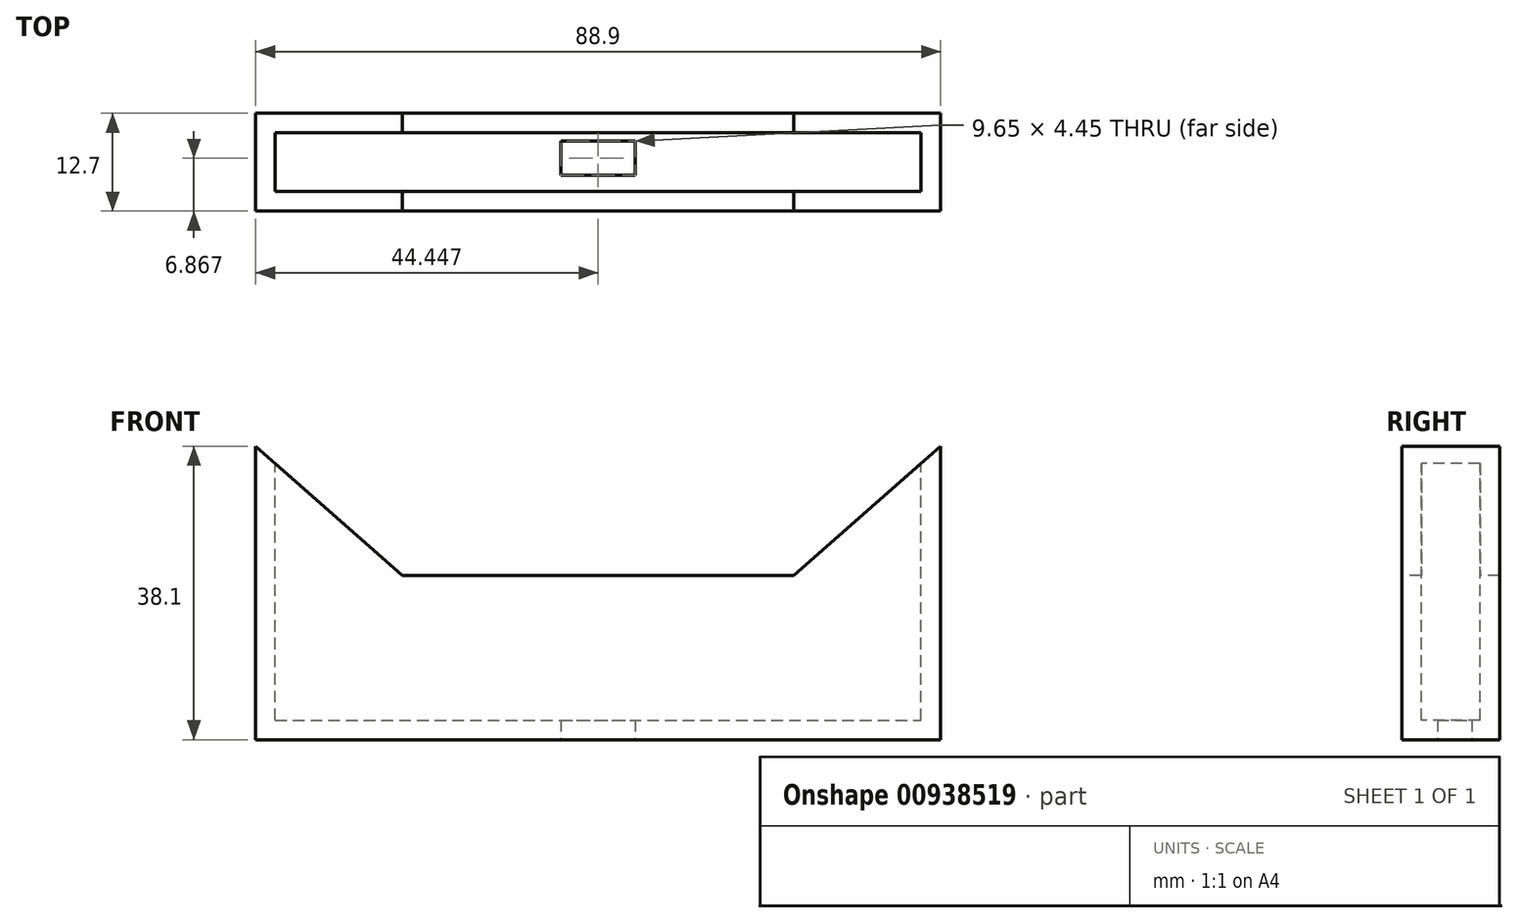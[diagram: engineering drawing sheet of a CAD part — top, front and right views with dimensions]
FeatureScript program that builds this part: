
annotation { "Feature Type Name" : "Feature", "Feature Type Description" : "" }
export const myFeature = defineFeature(function(context is Context, id is Id, definition is map)
    precondition{}
    {
        {
            var Q0;
            Q0=qCreatedBy(makeId("Front.planeOp"),FACE);
            var sketch = newSketch(context, id + "F0", { "sketchPlane" : qUnion([Q0])});
            skLineSegment(sketch, "E0", {"start": v(-47.41, 0) * mm, "end": v(41.49, 0) * mm});
            skLineSegment(sketch, "E1", {"start": v(41.49, 0) * mm, "end": v(41.49, 38.1) * mm});
            skLineSegment(sketch, "E2", {"start": v(-47.41, 0) * mm, "end": v(-47.41, 38.1) * mm});
            skLineSegment(sketch, "E3", {"start": v(-47.41, 38.1) * mm, "end": v(-28.36, 21.3) * mm});
            skLineSegment(sketch, "E4", {"start": v(-28.36, 21.3) * mm, "end": v(22.44, 21.3) * mm});
            skLineSegment(sketch, "E5", {"start": v(22.44, 21.3) * mm, "end": v(41.49, 38.1) * mm});
            skSolve(sketch);
        }
        {
            var Q0;
            Q0=makeQuery(id+"F0.imprint","IMPRINT",FACE,{"disambiguationData":[TD([[makeQuery(id+"F0.imprint","IMPRINT",EDGE,{"derivedFrom":sQuery(id+"F0.wireOp",EDGE,"E0")}),1.0]])]});
            extrude(context, id + "F1", {"entities" : qUnion([Q0]), "oppositeDirection" : true, "depth" : 12.7 * mm, "offsetDistance" : 25.4 * mm});
        }
        {
            var Q0;
            Q0=makeQuery(id+"F1.opExtrude","SWEPT_FACE",FACE,{"disambiguationData":[OSD([sQuery(id+"F0.wireOp",EDGE,"E4")])]});
            var Q1;
            Q1=makeQuery(id+"F1.opExtrude","SWEPT_FACE",FACE,{"disambiguationData":[OSD([sQuery(id+"F0.wireOp",EDGE,"E3")])]});
            var Q2;
            Q2=makeQuery(id+"F1.opExtrude","SWEPT_FACE",FACE,{"disambiguationData":[OSD([sQuery(id+"F0.wireOp",EDGE,"E5")])]});
            shell(context, id + "F2", {"entities" : qUnion([Q0, Q1, Q2]), "thickness" : 2.54 * mm});
        }
        {
            var Q0;
            Q0=qCreatedBy(makeId("Top.planeOp"),FACE);
            var sketch = newSketch(context, id + "F3", { "sketchPlane" : qUnion([Q0])});
            skLineSegment(sketch, "E6.bottom", {"start": v(-7.79, 4.64) * mm, "end": v(1.86, 4.64) * mm});
            skLineSegment(sketch, "E6.top", {"start": v(-7.79, 9.09) * mm, "end": v(1.86, 9.09) * mm});
            skLineSegment(sketch, "E6.left", {"start": v(-7.79, 4.64) * mm, "end": v(-7.79, 9.09) * mm});
            skLineSegment(sketch, "E6.right", {"start": v(1.86, 4.64) * mm, "end": v(1.86, 9.09) * mm});
            skLineSegment(sketch, "E7", {"start": v(-7.79, 9.09) * mm, "end": v(-47.41, 9.09) * mm, "construction": true});
            skLineSegment(sketch, "E8", {"start": v(1.86, 9.09) * mm, "end": v(41.49, 9.09) * mm, "construction": true});
            skSolve(sketch);
        }
        {
            var Q0;
            Q0=makeQuery(id+"F3.imprint","IMPRINT",FACE,{"disambiguationData":[TD([[makeQuery(id+"F3.imprint","IMPRINT",EDGE,{"derivedFrom":sQuery(id+"F3.wireOp",EDGE,"E6.bottom")}),1.0]])]});
            extrude(context, id + "F4", {"entities" : qUnion([Q0]), "operationType" : NewBodyOperationType.REMOVE, "depth" : 25.4 * mm, "offsetDistance" : 25.4 * mm});
        }
    });
